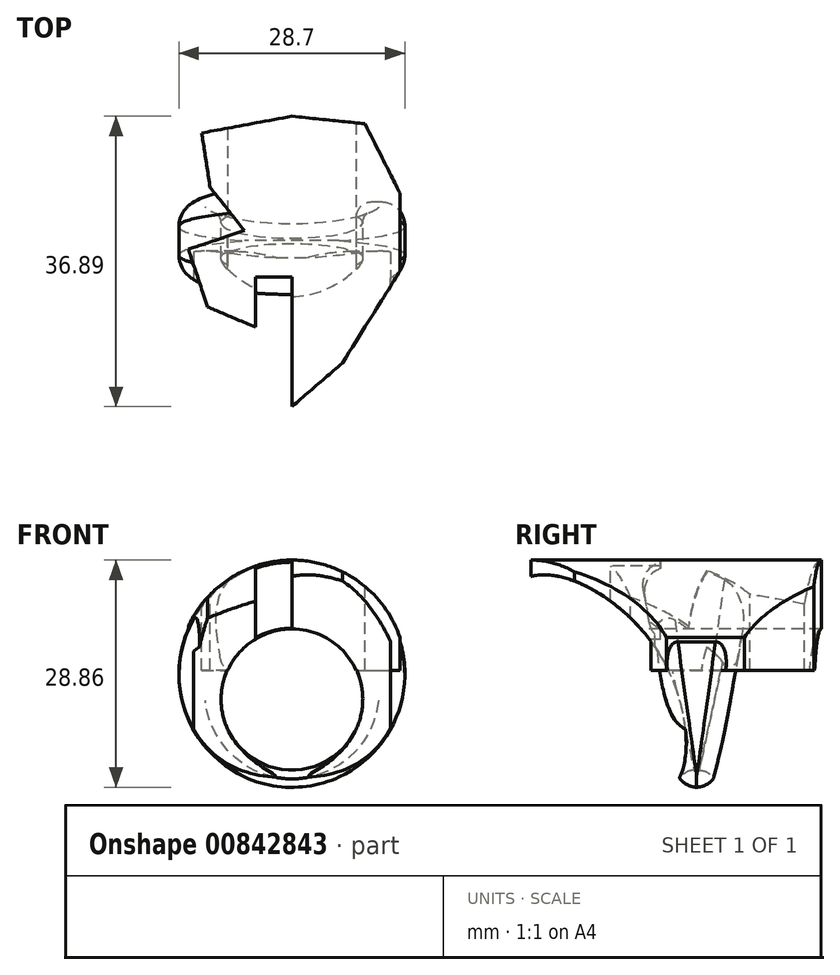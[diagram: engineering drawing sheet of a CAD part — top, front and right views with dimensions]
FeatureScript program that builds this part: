
annotation { "Feature Type Name" : "Feature", "Feature Type Description" : "" }
export const myFeature = defineFeature(function(context is Context, id is Id, definition is map)
    precondition{}
    {
        {
            var Q0;
            Q0=qCreatedBy(makeId("Front.planeOp"),FACE);
            var sketch = newSketch(context, id + "F0", { "sketchPlane" : qUnion([Q0])});
            skCircle(sketch, "E0", {"center": v(0, 0) * mm, "radius": 9 * mm});
            skCircle(sketch, "E1", {"center": v(0, 3.17) * mm, "radius": 14.35 * mm});
            skSolve(sketch);
        }
        {
            var Q0;
            Q0=makeQuery(id+"F0.imprint","IMPRINT",FACE,{"disambiguationData":[TD([[makeQuery(id+"F0.imprint","IMPRINT",EDGE,{"derivedFrom":sQuery(id+"F0.wireOp",EDGE,"E0")}),-1.0]])]});
            extrude(context, id + "F1", {"entities" : qUnion([Q0]), "depth" : 15 * mm, "offsetDistance" : 25 * mm});
        }
        {
            var Q0;
            Q0=qCreatedBy(makeId("Right.planeOp"),FACE);
            var sketch = newSketch(context, id + "F2", { "sketchPlane" : qUnion([Q0])});
            skLineSegment(sketch, "E2.bottom", {"start": v(-15.87, 22.88) * mm, "end": v(-32.27, 20) * mm});
            skLineSegment(sketch, "E2.top", {"start": v(-9.26, -14.62) * mm, "end": v(-25.66, -17.51) * mm});
            skLineSegment(sketch, "E2.left", {"start": v(-15.87, 22.88) * mm, "end": v(-9.26, -14.62) * mm});
            skLineSegment(sketch, "E2.right", {"start": v(-32.27, 20) * mm, "end": v(-25.66, -17.51) * mm});
            skLineSegment(sketch, "E3.bottom", {"start": v(15.52, 21.83) * mm, "end": v(1.07, 24.37) * mm});
            skLineSegment(sketch, "E3.top", {"start": v(8.64, -17.17) * mm, "end": v(-5.8, -14.62) * mm});
            skLineSegment(sketch, "E3.left", {"start": v(15.52, 21.83) * mm, "end": v(8.64, -17.17) * mm});
            skLineSegment(sketch, "E3.right", {"start": v(1.07, 24.37) * mm, "end": v(-5.8, -14.62) * mm});
            skSolve(sketch);
        }
        {
            var Q0;
            Q0=makeQuery(id+"F2.imprint","IMPRINT",FACE,{"disambiguationData":[TD([[makeQuery(id+"F2.imprint","IMPRINT",EDGE,{"derivedFrom":sQuery(id+"F2.wireOp",EDGE,"E3.bottom")}),1.0]])]});
            var Q1;
            Q1=makeQuery(id+"F2.imprint","IMPRINT",FACE,{"disambiguationData":[TD([[makeQuery(id+"F2.imprint","IMPRINT",EDGE,{"derivedFrom":sQuery(id+"F2.wireOp",EDGE,"E2.bottom")}),1.0]])]});
            extrude(context, id + "F3", {"entities" : qUnion([Q0, Q1]), "operationType" : NewBodyOperationType.REMOVE, "depth" : 40 * mm, "offsetDistance" : 25 * mm, "symmetric" : true});
        }
        {
            var Q0;
            Q0=makeQuery(id+"F3.boolean.opBoolean","INTERSECT",EDGE,{"derivedFrom":[makeQuery(id+"F1.opExtrude","SWEPT_FACE",FACE,{"disambiguationData":[OSD([sQuery(id+"F0.wireOp",EDGE,"E0")])]}),makeQuery(id+"F3.opExtrude","SWEPT_FACE",FACE,{"disambiguationData":[OSD([sQuery(id+"F2.wireOp",EDGE,"E2.left")])]})]});
            var Q1;
            Q1=makeQuery(id+"F3.boolean.opBoolean","INTERSECT",EDGE,{"derivedFrom":[makeQuery(id+"F1.opExtrude","SWEPT_FACE",FACE,{"disambiguationData":[OSD([sQuery(id+"F0.wireOp",EDGE,"E0")])]}),makeQuery(id+"F3.opExtrude","SWEPT_FACE",FACE,{"disambiguationData":[OSD([sQuery(id+"F2.wireOp",EDGE,"E3.right")])]})]});
            fillet(context, id + "F4", {"entities" : qUnion([Q0, Q1]), "radius" : 2 * mm, "allowEdgeOverflow" : false});
        }
        {
            var Q0;
            Q0=makeQuery(id+"F3.boolean.opBoolean","INTERSECT",EDGE,{"derivedFrom":[makeQuery(id+"F1.opExtrude","SWEPT_FACE",FACE,{"disambiguationData":[OSD([sQuery(id+"F0.wireOp",EDGE,"E1")])]}),makeQuery(id+"F3.opExtrude","SWEPT_FACE",FACE,{"disambiguationData":[OSD([sQuery(id+"F2.wireOp",EDGE,"E2.left")])]})]});
            var Q1;
            Q1=makeQuery(id+"F3.boolean.opBoolean","INTERSECT",EDGE,{"derivedFrom":[makeQuery(id+"F1.opExtrude","SWEPT_FACE",FACE,{"disambiguationData":[OSD([sQuery(id+"F0.wireOp",EDGE,"E1")])]}),makeQuery(id+"F3.opExtrude","SWEPT_FACE",FACE,{"disambiguationData":[OSD([sQuery(id+"F2.wireOp",EDGE,"E3.right")])]})]});
            fillet(context, id + "F5", {"entities" : qUnion([Q0, Q1]), "radius" : 3 * mm, "allowEdgeOverflow" : false});
        }
        {
            var Q0;
            Q0=qCreatedBy(makeId("Top.planeOp"),FACE);
            cPlane(context, id + "F6", {"entities" : qUnion([Q0]), "cplaneType" : CPlaneType.OFFSET, "offset" : 17.7 * mm, "width" : 150 * mm, "height" : 150 * mm});
        }
        {
            var Q0;
            Q0=qCreatedBy(id+"F6.planeOp",FACE);
            var sketch = newSketch(context, id + "F7", { "sketchPlane" : qUnion([Q0])});
            skLineSegment(sketch, "E4", {"start": v(0, 8.29) * mm, "end": v(9.28, 7.33) * mm});
            skLineSegment(sketch, "E5", {"start": v(9.28, 7.33) * mm, "end": v(13.74, -1.5) * mm});
            skLineSegment(sketch, "E6", {"start": v(13.74, -1.5) * mm, "end": v(13.74, -11.38) * mm});
            skLineSegment(sketch, "E7", {"start": v(13.74, -11.38) * mm, "end": v(6.4, -23.07) * mm});
            skLineSegment(sketch, "E8", {"start": v(6.4, -23.07) * mm, "end": v(0, -28.6) * mm});
            skLineSegment(sketch, "E9", {"start": v(0, -28.6) * mm, "end": v(0, -12.12) * mm});
            skLineSegment(sketch, "E10", {"start": v(0, -12.12) * mm, "end": v(-4.65, -12.12) * mm});
            skLineSegment(sketch, "E11", {"start": v(-4.65, -12.12) * mm, "end": v(-4.65, -18.5) * mm});
            skLineSegment(sketch, "E12", {"start": v(-4.65, -18.5) * mm, "end": v(-10.7, -15.95) * mm});
            skLineSegment(sketch, "E13", {"start": v(-10.7, -15.95) * mm, "end": v(-13.15, -8.61) * mm});
            skLineSegment(sketch, "E14", {"start": v(-13.15, -8.61) * mm, "end": v(-6.04, -6.24) * mm});
            skLineSegment(sketch, "E15", {"start": v(-6.04, -6.24) * mm, "end": v(-10.4, -0.75) * mm});
            skLineSegment(sketch, "E16", {"start": v(-10.4, -0.75) * mm, "end": v(-11.45, 6.16) * mm});
            skLineSegment(sketch, "E17", {"start": v(-11.45, 6.16) * mm, "end": v(0, 8.29) * mm});
            skSolve(sketch);
        }
        {
            var Q0;
            Q0 = qSketchRegion(id + "F7", true);
            extrude(context, id + "F8", {"entities" : qUnion([Q0]), "operationType" : NewBodyOperationType.ADD, "oppositeDirection" : true, "depth" : 14 * mm, "offsetDistance" : 25 * mm});
        }
        {
            var Q0;
            Q0=qCreatedBy(makeId("Front.planeOp"),FACE);
            var sketch = newSketch(context, id + "F9", { "sketchPlane" : qUnion([Q0])});
            skCircle(sketch, "E18", {"center": v(0, 0) * mm, "radius": 8.95 * mm});
            skSolve(sketch);
        }
        {
            var Q0;
            Q0 = qSketchRegion(id + "F9", true);
            extrude(context, id + "F10", {"entities" : qUnion([Q0]), "operationType" : NewBodyOperationType.REMOVE, "oppositeDirection" : true, "depth" : 40 * mm, "offsetDistance" : 25 * mm, "symmetric" : true});
        }
        {
            var Q0;
            Q0=qCreatedBy(makeId("Front.planeOp"),FACE);
            var sketch = newSketch(context, id + "F11", { "sketchPlane" : qUnion([Q0])});
            skCircle(sketch, "E19", {"center": v(0, 3.18) * mm, "radius": 14.51 * mm});
            skSolve(sketch);
        }
        {
            var Q0;
            Q0 = qSketchRegion(id + "F11", true);
            extrude(context, id + "F12", {"entities" : qUnion([Q0]), "operationType" : NewBodyOperationType.INTERSECT, "oppositeDirection" : true, "depth" : 67.8 * mm, "offsetDistance" : 25 * mm, "symmetric" : true});
        }
        {
            var Q0;
            Q0=qCreatedBy(makeId("Right.planeOp"),FACE);
            var sketch = newSketch(context, id + "F13", { "sketchPlane" : qUnion([Q0])});
            skFitSpline(sketch, "E20", {"points": [v(-9.91, -10.31) * mm, v(-12.86, 6.7) * mm, v(-28.8, 15.54) * mm, v(-32.41, 4.82) * mm, v(-17.14, -11.79) * mm, v(-9.91, -10.31) * mm]});
            skSolve(sketch);
        }
        {
            var Q0;
            Q0 = qSketchRegion(id + "F13", true);
            extrude(context, id + "F14", {"entities" : qUnion([Q0]), "operationType" : NewBodyOperationType.REMOVE, "depth" : 25 * mm, "offsetDistance" : 25 * mm, "symmetric" : true});
        }
    });
